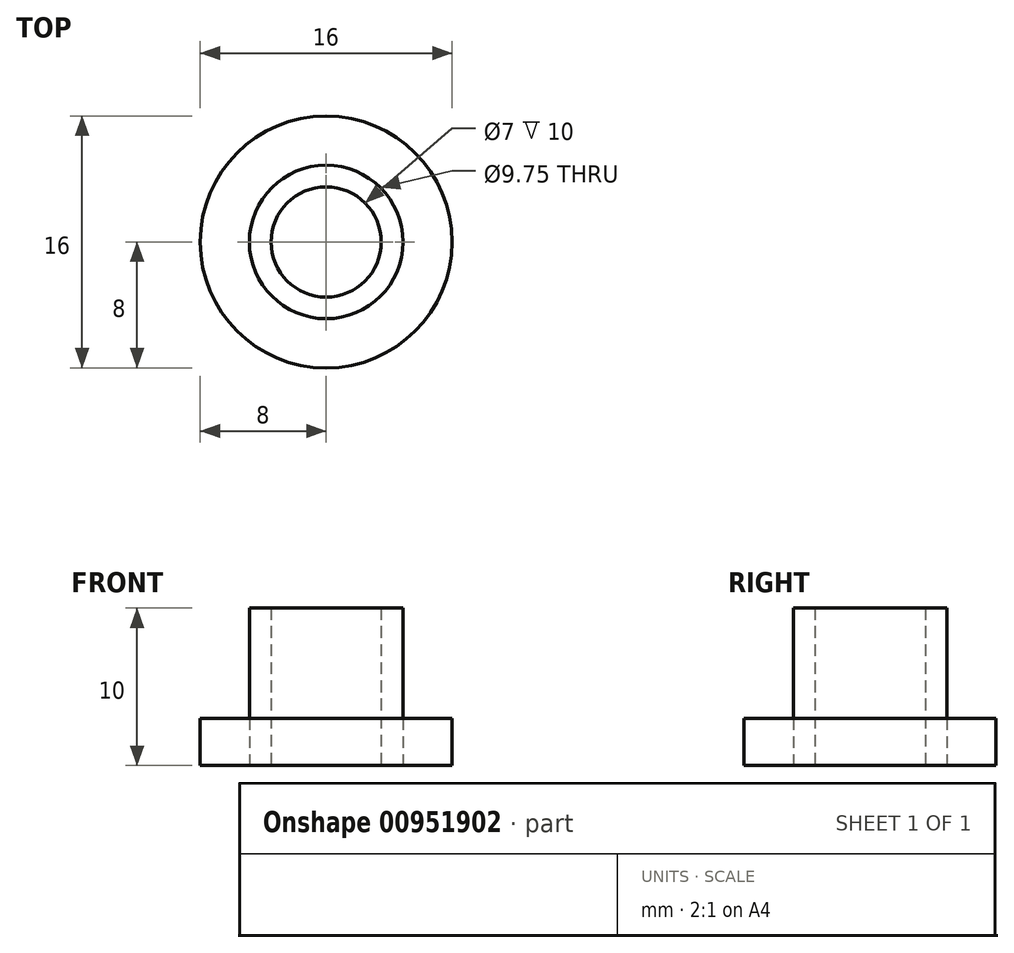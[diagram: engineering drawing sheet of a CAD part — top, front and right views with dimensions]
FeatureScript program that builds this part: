
annotation { "Feature Type Name" : "Feature", "Feature Type Description" : "" }
export const myFeature = defineFeature(function(context is Context, id is Id, definition is map)
    precondition{}
    {
        {
            var Q0;
            Q0=qCreatedBy(makeId("Top.planeOp"),FACE);
            var sketch = newSketch(context, id + "F0", { "sketchPlane" : qUnion([Q0])});
            skCircle(sketch, "E0", {"center": v(-9.5, 0) * mm, "radius": 4.88 * mm});
            skCircle(sketch, "E1", {"center": v(-9.5, 0) * mm, "radius": 8 * mm});
            skCircle(sketch, "E2", {"center": v(-9.5, 0) * mm, "radius": 3.5 * mm});
            skPoint(sketch, "E3.center.orphan", {"position": v(-39.15, 0) * mm});
            skSolve(sketch);
        }
        {
            var Q0;
            Q0=makeQuery(id+"F0.imprint","IMPRINT",FACE,{"disambiguationData":[TD([[makeQuery(id+"F0.imprint","IMPRINT",EDGE,{"derivedFrom":sQuery(id+"F0.wireOp",EDGE,"OktzW2Pz-47kU-gWwa-kMjT-OYjADVK3GVA4")}),1.0]])]});
            var Q1;
            Q1=makeQuery(id+"F0.imprint","IMPRINT",FACE,{"disambiguationData":[TD([[makeQuery(id+"F0.imprint","IMPRINT",EDGE,{"derivedFrom":sQuery(id+"F0.wireOp",EDGE,"E0")}),-1.0]])]});
            extrude(context, id + "F1", {"entities" : qUnion([Q0, Q1]), "depth" : 3 * mm, "offsetDistance" : 25 * mm});
        }
        {
            var Q0;
            Q0=makeQuery(id+"F0.imprint","IMPRINT",FACE,{"disambiguationData":[TD([[makeQuery(id+"F0.imprint","IMPRINT",EDGE,{"derivedFrom":sQuery(id+"F0.wireOp",EDGE,"OktzW2Pz-47kU-gWwa-kMjT-OYjADVK3GVA4")}),-1.0]])]});
            var Q1;
            Q1=makeQuery(id+"F0.imprint","IMPRINT",FACE,{"disambiguationData":[TD([[makeQuery(id+"F0.imprint","IMPRINT",EDGE,{"derivedFrom":sQuery(id+"F0.wireOp",EDGE,"E0")}),1.0]])]});
            extrude(context, id + "F2", {"entities" : qUnion([Q0, Q1]), "depth" : 10 * mm, "offsetDistance" : 25 * mm});
        }
    });
